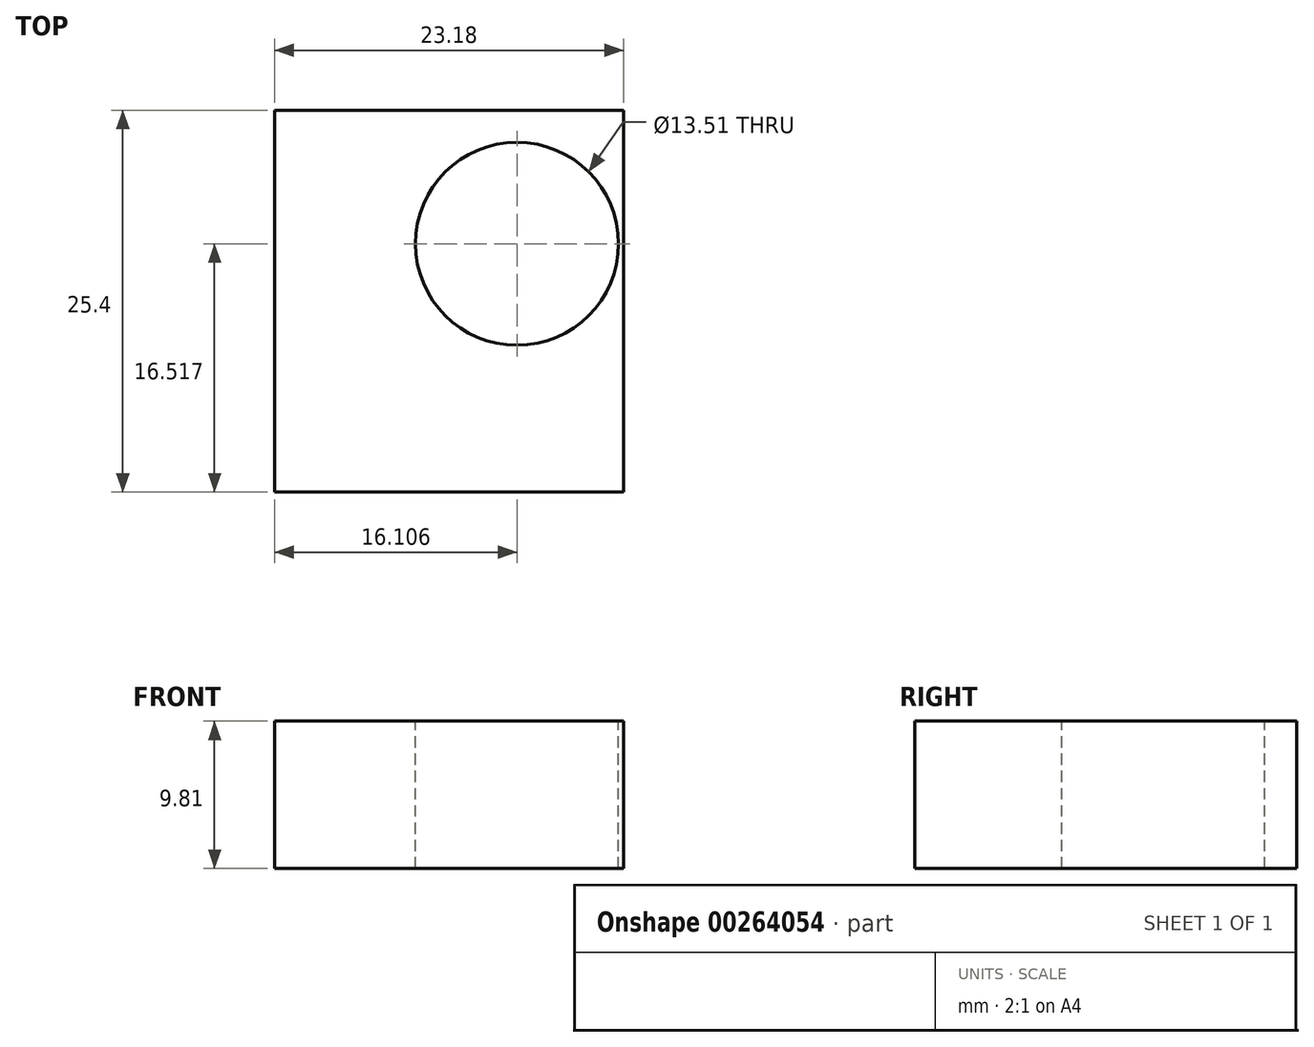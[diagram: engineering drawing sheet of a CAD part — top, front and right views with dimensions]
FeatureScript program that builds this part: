
annotation { "Feature Type Name" : "Feature", "Feature Type Description" : "" }
export const myFeature = defineFeature(function(context is Context, id is Id, definition is map)
    precondition{}
    {
        {
            var Q0;
            Q0=qCreatedBy(makeId("Front.planeOp"),FACE);
            var sketch = newSketch(context, id + "F0", { "sketchPlane" : qUnion([Q0])});
            skLineSegment(sketch, "E0.bottom", {"start": v(31.2, 43.7) * mm, "end": v(54.4, 43.7) * mm});
            skLineSegment(sketch, "E0.top", {"start": v(31.2, 33.88) * mm, "end": v(54.4, 33.88) * mm});
            skLineSegment(sketch, "E0.left", {"start": v(31.2, 43.7) * mm, "end": v(31.2, 33.88) * mm});
            skLineSegment(sketch, "E0.right", {"start": v(54.4, 43.7) * mm, "end": v(54.4, 33.88) * mm});
            skSolve(sketch);
        }
        {
            var Q0;
            Q0=makeQuery(id+"F0.imprint","IMPRINT",FACE,{"disambiguationData":[TD([[makeQuery(id+"F0.imprint","IMPRINT",EDGE,{"derivedFrom":sQuery(id+"F0.wireOp",EDGE,"E0.bottom")}),-1.0]])]});
            extrude(context, id + "F1", {"entities" : qUnion([Q0]), "depth" : 25.4 * mm});
        }
        {
            var Q0;
            Q0=makeQuery(id+"F1.opExtrude","SWEPT_FACE",FACE,{"disambiguationData":[OSD([sQuery(id+"F0.wireOp",EDGE,"E0.bottom")])]});
            var sketch = newSketch(context, id + "F2", { "sketchPlane" : qUnion([Q0])});
            skCircle(sketch, "E1", {"center": v(49.04, -4.68) * mm, "radius": 3.68 * mm});
            skCircle(sketch, "E2", {"center": v(36.56, -16.71) * mm, "radius": 5.35 * mm});
            skSolve(sketch);
        }
        {
            var Q0;
            Q0=makeQuery(id+"F2.imprint","IMPRINT",FACE,{"disambiguationData":[TD([[makeQuery(id+"F2.imprint","IMPRINT",EDGE,{"derivedFrom":sQuery(id+"F2.wireOp",EDGE,"E2")}),1.0]])]});
            extrude(context, id + "F3", {"entities" : qUnion([Q0]), "operationType" : NewBodyOperationType.REMOVE, "depth" : 25.4 * mm});
        }
        {
            var Q0;
            Q0=makeQuery(id+"F1.opExtrude","SWEPT_FACE",FACE,{"disambiguationData":[OSD([sQuery(id+"F0.wireOp",EDGE,"E0.bottom")])]});
            var sketch = newSketch(context, id + "F4", { "sketchPlane" : qUnion([Q0])});
            skCircle(sketch, "E3", {"center": v(47.32, -8.88) * mm, "radius": 6.75 * mm});
            skSolve(sketch);
        }
        {
            var Q0;
            Q0=makeQuery(id+"F4.imprint","IMPRINT",FACE,{"disambiguationData":[TD([[makeQuery(id+"F4.imprint","IMPRINT",EDGE,{"derivedFrom":sQuery(id+"F4.wireOp",EDGE,"E3")}),1.0]])]});
            extrude(context, id + "F5", {"entities" : qUnion([Q0]), "operationType" : NewBodyOperationType.REMOVE, "oppositeDirection" : true, "depth" : 25.4 * mm});
        }
    });
